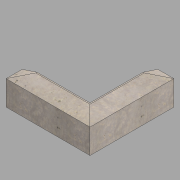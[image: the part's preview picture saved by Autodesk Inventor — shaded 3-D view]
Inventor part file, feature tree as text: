
AUTODESK INVENTOR PART (.ipt)
format: ipt  version: 2022.1 (Build 261234020, 234B)  size: 147,968 bytes
history: native  units: in
note: dims shown in document units (in); Inventor stores cm internally (conversion verified against a paired STEP export)
features: sketch x5, extrude x3, sweep x1
ambient origin geometry x8: Origin, YZ Plane, XZ Plane, XY Plane, X Axis, Y Axis, Z Axis, Center Point
bodies: Solid1 (feature_tree)
feature tree (9):
  extrude  "Extrusion1"  Depth=27.5in
  sweep  "Sweep1"
  extrude  "Extrusion2"  Depth=34.0in
  extrude  "Extrusion3"  Depth=12.0in
  sketch  "Sketch1"  dims[d1=27.5in d2=27.5in]
  sketch  "Sketch2"  dims[d3=6.5in d4=6.5in]
  sketch  "3D Sketch1"
  sketch  "Sketch3"  dims[d5=34.0in d6=34.0in]
  sketch  "Sketch4"  dims[d7=12.0in d8=0.0in d9=0.5in d10=2.0in d11=0.0in d12=0.0in d13=6.0in d14=2.0in d15=0.0in d16=0.0in d17=6.0in d18=2.0in d19=0.0in d20=0.0in]
